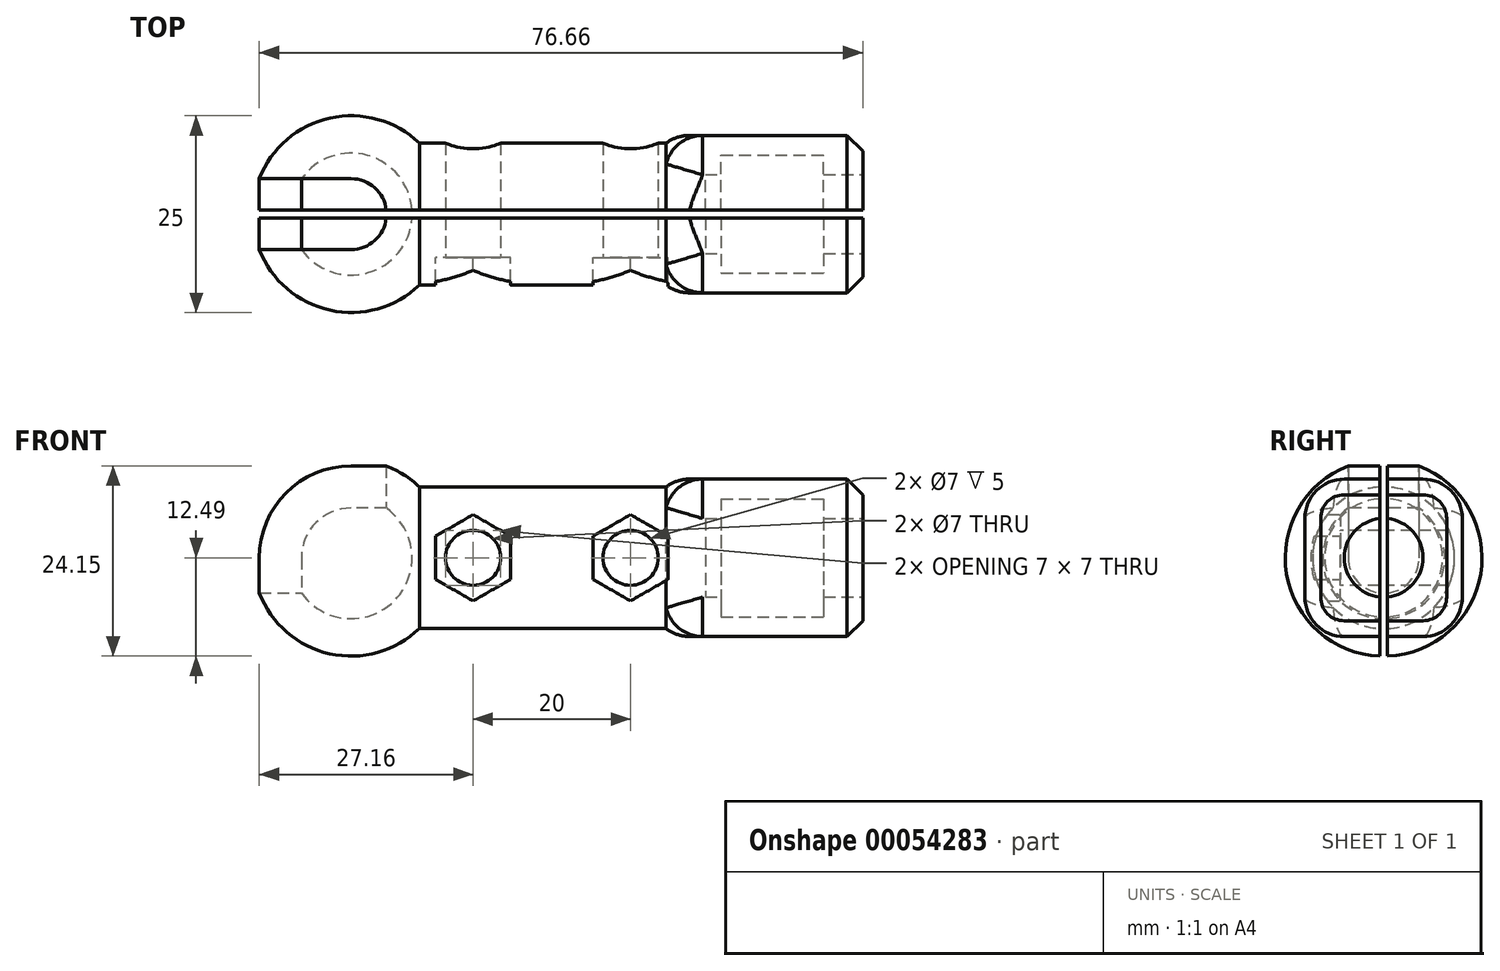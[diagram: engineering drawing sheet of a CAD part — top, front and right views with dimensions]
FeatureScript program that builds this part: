
annotation { "Feature Type Name" : "Feature", "Feature Type Description" : "" }
export const myFeature = defineFeature(function(context is Context, id is Id, definition is map)
    precondition{}
    {
        {
            var Q0;
            Q0=qCreatedBy(makeId("Top.planeOp"),FACE);
            var sketch = newSketch(context, id + "F0", { "sketchPlane" : qUnion([Q0])});
            skLineSegment(sketch, "E0.bottom", {"start": v(0, 0) * mm, "end": v(25, 0) * mm});
            skLineSegment(sketch, "E0.top", {"start": v(0, 25) * mm, "end": v(25, 25) * mm});
            skLineSegment(sketch, "E0.left", {"start": v(0, 0) * mm, "end": v(0, 25) * mm});
            skLineSegment(sketch, "E0.right", {"start": v(25, 0) * mm, "end": v(25, 25) * mm});
            skSolve(sketch);
        }
        {
            var Q0;
            Q0 = qSketchRegion(id + "F0", true);
            extrude(context, id + "F1", {"entities" : qUnion([Q0]), "depth" : 25 * mm});
        }
        {
            var Q0;
            Q0=makeQuery(id+"F1.opExtrude","CAP_EDGE",EDGE,{"disambiguationData":[OSD([sQuery(id+"F0.wireOp",EDGE,"E0.left")])],"isStart":false});
            var Q1;
            Q1=makeQuery(id+"F1.opExtrude","CAP_EDGE",EDGE,{"disambiguationData":[OSD([sQuery(id+"F0.wireOp",EDGE,"E0.right")])],"isStart":false});
            var Q2;
            Q2=makeQuery(id+"F1.opExtrude","CAP_EDGE",EDGE,{"disambiguationData":[OSD([sQuery(id+"F0.wireOp",EDGE,"E0.right")])],"isStart":true});
            var Q3;
            Q3=makeQuery(id+"F1.opExtrude","CAP_FACE",FACE,{"disambiguationData":[OSD([sQuery(id+"F0.wireOp",EDGE,"E0.bottom"),sQuery(id+"F0.wireOp",EDGE,"E0.top"),sQuery(id+"F0.wireOp",EDGE,"E0.left"),sQuery(id+"F0.wireOp",EDGE,"E0.right")])],"isStart":true});
            var Q4;
            Q4=makeQuery(id+"F1.opExtrude","SWEPT_EDGE",EDGE,{"disambiguationData":[OSD([sQuery(id+"F0.wireOp",EDGE,"E0.bottom"),sQuery(id+"F0.wireOp",EDGE,"E0.left")])]});
            var Q5;
            Q5=makeQuery(id+"F1.opExtrude","SWEPT_EDGE",EDGE,{"disambiguationData":[OSD([sQuery(id+"F0.wireOp",EDGE,"E0.top"),sQuery(id+"F0.wireOp",EDGE,"E0.left")])]});
            var Q6;
            Q6=makeQuery(id+"F1.opExtrude","CAP_EDGE",EDGE,{"disambiguationData":[OSD([sQuery(id+"F0.wireOp",EDGE,"E0.top")])],"isStart":true});
            var Q7;
            Q7=makeQuery(id+"F1.opExtrude","CAP_EDGE",EDGE,{"disambiguationData":[OSD([sQuery(id+"F0.wireOp",EDGE,"E0.left")])],"isStart":true});
            var Q8;
            Q8=makeQuery(id+"F1.opExtrude","CAP_EDGE",EDGE,{"disambiguationData":[OSD([sQuery(id+"F0.wireOp",EDGE,"E0.bottom")])],"isStart":false});
            var Q9;
            Q9=makeQuery(id+"F1.opExtrude","CAP_EDGE",EDGE,{"disambiguationData":[OSD([sQuery(id+"F0.wireOp",EDGE,"E0.top")])],"isStart":false});
            var Q10;
            Q10=makeQuery(id+"F1.opExtrude","SWEPT_EDGE",EDGE,{"disambiguationData":[OSD([sQuery(id+"F0.wireOp",EDGE,"E0.top"),sQuery(id+"F0.wireOp",EDGE,"E0.right")])]});
            var Q11;
            Q11=makeQuery(id+"F1.opExtrude","SWEPT_EDGE",EDGE,{"disambiguationData":[OSD([sQuery(id+"F0.wireOp",EDGE,"E0.bottom"),sQuery(id+"F0.wireOp",EDGE,"E0.right")])]});
            fillet(context, id + "F2", {"entities" : qUnion([Q0, Q1, Q2, Q3, Q4, Q5, Q6, Q7, Q8, Q9, Q10, Q11]), "radius" : 12.5 * mm, "tangentPropagation" : true, "allowEdgeOverflow" : false});
        }
        {
            var Q0;
            Q0=qCreatedBy(makeId("Right.planeOp"),FACE);
            cPlane(context, id + "F3", {"entities" : qUnion([Q0]), "cplaneType" : CPlaneType.OFFSET, "offset" : 12.5 * mm, "width" : 150 * mm, "height" : 150 * mm});
        }
        {
            var Q0;
            Q0=qCreatedBy(id+"F3.planeOp",FACE);
            var sketch = newSketch(context, id + "F4", { "sketchPlane" : qUnion([Q0])});
            skCircle(sketch, "E1", {"center": v(12.5, 12.5) * mm, "radius": 9 * mm});
            skSolve(sketch);
        }
        {
            var Q0;
            Q0 = qSketchRegion(id + "F4", true);
            extrude(context, id + "F5", {"entities" : qUnion([Q0]), "operationType" : NewBodyOperationType.ADD, "depth" : 40 * mm});
        }
        {
            var Q0;
            Q0=makeQuery(id+"F5.opExtrude","CAP_FACE",FACE,{"disambiguationData":[OSD([sQuery(id+"F4.wireOp",EDGE,"E1")])],"isStart":false});
            var sketch = newSketch(context, id + "F6", { "sketchPlane" : qUnion([Q0])});
            skLineSegment(sketch, "E2.bottom", {"start": v(2.5, 22.5) * mm, "end": v(22.5, 22.5) * mm});
            skLineSegment(sketch, "E2.top", {"start": v(2.5, 2.5) * mm, "end": v(22.5, 2.5) * mm});
            skLineSegment(sketch, "E2.left", {"start": v(2.5, 22.5) * mm, "end": v(2.5, 2.5) * mm});
            skLineSegment(sketch, "E2.right", {"start": v(22.5, 22.5) * mm, "end": v(22.5, 2.5) * mm});
            skPoint(sketch, "E3", {"position": v(12.5, 12.5) * mm});
            skSolve(sketch);
        }
        {
            var Q0;
            Q0 = qSketchRegion(id + "F6", true);
            extrude(context, id + "F7", {"entities" : qUnion([Q0]), "operationType" : NewBodyOperationType.ADD, "depth" : 25 * mm});
        }
        {
            var Q0;
            Q0=makeQuery(id+"F7.opExtrude","SWEPT_EDGE",EDGE,{"disambiguationData":[OSD([sQuery(id+"F6.wireOp",EDGE,"E2.bottom"),sQuery(id+"F6.wireOp",EDGE,"E2.left")])]});
            var Q1;
            Q1=makeQuery(id+"F7.opExtrude","SWEPT_EDGE",EDGE,{"disambiguationData":[OSD([sQuery(id+"F6.wireOp",EDGE,"E2.bottom"),sQuery(id+"F6.wireOp",EDGE,"E2.right")])]});
            var Q2;
            Q2=makeQuery(id+"F7.opExtrude","SWEPT_EDGE",EDGE,{"disambiguationData":[OSD([sQuery(id+"F6.wireOp",EDGE,"E2.top"),sQuery(id+"F6.wireOp",EDGE,"E2.right")])]});
            var Q3;
            Q3=makeQuery(id+"F7.opExtrude","SWEPT_EDGE",EDGE,{"disambiguationData":[OSD([sQuery(id+"F6.wireOp",EDGE,"E2.top"),sQuery(id+"F6.wireOp",EDGE,"E2.left")])]});
            fillet(context, id + "F8", {"entities" : qUnion([Q0, Q1, Q2, Q3]), "radius" : 5 * mm, "tangentPropagation" : true, "allowEdgeOverflow" : false});
        }
        {
            var Q0;
            Q0=qCreatedBy(makeId("Top.planeOp"),FACE);
            var sketch = newSketch(context, id + "F9", { "sketchPlane" : qUnion([Q0])});
            skLineSegment(sketch, "E4.bottom", {"start": v(0, 12) * mm, "end": v(80, 12) * mm});
            skLineSegment(sketch, "E4.top", {"start": v(0, 13) * mm, "end": v(80, 13) * mm});
            skLineSegment(sketch, "E4.left", {"start": v(0, 12) * mm, "end": v(0, 13) * mm});
            skLineSegment(sketch, "E4.right", {"start": v(80, 12) * mm, "end": v(80, 13) * mm});
            skSolve(sketch);
        }
        {
            var Q0;
            Q0 = qSketchRegion(id + "F9", true);
            extrude(context, id + "F10", {"entities" : qUnion([Q0]), "operationType" : NewBodyOperationType.REMOVE, "endBound" : BoundingType.THROUGH_ALL, "depth" : 29.4 * mm});
        }
        {
            var Q0;
            {var subQ0=sQuery(id+"F6.wireOp",EDGE,"E2.right");var subQ1=sQuery(id+"F6.wireOp",EDGE,"E2.bottom");Q0=makeQuery(id+"F8.opFillet","BLEND_EDGE",EDGE,{"blendedFrom":[makeQuery(id+"F7.opExtrude","SWEPT_EDGE",EDGE,{"disambiguationData":[OSD([subQ1,subQ0])]}),makeQuery(id+"F7.opExtrude","CAP_FACE",FACE,{"disambiguationData":[OSD([subQ1,sQuery(id+"F6.wireOp",EDGE,"E2.top"),sQuery(id+"F6.wireOp",EDGE,"E2.left"),subQ0])],"isStart":true})],"blendedInto":[makeQuery(id+"F7.opExtrude","CAP_FACE",FACE,{"disambiguationData":[OSD([subQ1,sQuery(id+"F6.wireOp",EDGE,"E2.top"),sQuery(id+"F6.wireOp",EDGE,"E2.left"),subQ0])],"isStart":true})]});}
            var Q1;
            {var subQ0=sQuery(id+"F6.wireOp",EDGE,"E2.left");var subQ1=sQuery(id+"F6.wireOp",EDGE,"E2.bottom");Q1=makeQuery(id+"F8.opFillet","BLEND_EDGE",EDGE,{"blendedFrom":[makeQuery(id+"F7.opExtrude","SWEPT_EDGE",EDGE,{"disambiguationData":[OSD([subQ1,subQ0])]}),makeQuery(id+"F7.opExtrude","CAP_FACE",FACE,{"disambiguationData":[OSD([subQ1,sQuery(id+"F6.wireOp",EDGE,"E2.top"),subQ0,sQuery(id+"F6.wireOp",EDGE,"E2.right")])],"isStart":true})],"blendedInto":[makeQuery(id+"F7.opExtrude","CAP_FACE",FACE,{"disambiguationData":[OSD([subQ1,sQuery(id+"F6.wireOp",EDGE,"E2.top"),subQ0,sQuery(id+"F6.wireOp",EDGE,"E2.right")])],"isStart":true})]});}
            fillet(context, id + "F11", {"entities" : qUnion([Q0, Q1]), "radius" : 5 * mm, "tangentPropagation" : true, "allowEdgeOverflow" : false});
        }
        {
            var Q0;
            {var subQ0=sQuery(id+"F6.wireOp",EDGE,"E2.left");var subQ1=sQuery(id+"F6.wireOp",EDGE,"E2.bottom");var subQ2=sQuery(id+"F6.wireOp",EDGE,"E2.top");Q0=makeQuery(id+"F10.boolean.opBoolean","SPLIT",FACE,{"disambiguationData":[TD([makeQuery(id+"F7.opExtrude","SWEPT_FACE",FACE,{"disambiguationData":[OSD([subQ0])]})])],"derivedFrom":makeQuery(id+"F7.opExtrude","CAP_FACE",FACE,{"disambiguationData":[OSD([subQ1,subQ2,subQ0,sQuery(id+"F6.wireOp",EDGE,"E2.right")])],"isStart":false})});}
            var sketch = newSketch(context, id + "F12", { "sketchPlane" : qUnion([Q0])});
            skCircle(sketch, "E5", {"center": v(12.5, 12.5) * mm, "radius": 5 * mm});
            skSolve(sketch);
        }
        {
            var Q0;
            Q0 = qSketchRegion(id + "F12", true);
            extrude(context, id + "F13", {"entities" : qUnion([Q0]), "operationType" : NewBodyOperationType.REMOVE, "oppositeDirection" : true, "depth" : 20 * mm});
        }
        {
            var Q0;
            {var subQ0=sQuery(id+"F6.wireOp",EDGE,"E2.right");var subQ1=sQuery(id+"F6.wireOp",EDGE,"E2.bottom");var subQ2=sQuery(id+"F6.wireOp",EDGE,"E2.top");Q0=makeQuery(id+"F10.boolean.opBoolean","SPLIT",FACE,{"disambiguationData":[TD([makeQuery(id+"F7.opExtrude","SWEPT_FACE",FACE,{"disambiguationData":[OSD([subQ0])]})])],"derivedFrom":makeQuery(id+"F7.opExtrude","CAP_FACE",FACE,{"disambiguationData":[OSD([subQ1,subQ2,sQuery(id+"F6.wireOp",EDGE,"E2.left"),subQ0])],"isStart":false})});}
            cPlane(context, id + "F14", {"entities" : qUnion([Q0]), "cplaneType" : CPlaneType.OFFSET, "offset" : 5 * mm, "oppositeDirection" : true, "width" : 150 * mm, "height" : 150 * mm});
        }
        {
            var Q0;
            Q0=qCreatedBy(id+"F14.planeOp",FACE);
            var sketch = newSketch(context, id + "F15", { "sketchPlane" : qUnion([Q0])});
            skCircle(sketch, "E6", {"center": v(12.5, 12.5) * mm, "radius": 7.5 * mm});
            skSolve(sketch);
        }
        {
            var Q0;
            Q0 = qSketchRegion(id + "F15", true);
            extrude(context, id + "F16", {"entities" : qUnion([Q0]), "operationType" : NewBodyOperationType.REMOVE, "oppositeDirection" : true, "depth" : 13 * mm});
        }
        {
            var Q0;
            Q0=qCreatedBy(id+"F3.planeOp",FACE);
            var sketch = newSketch(context, id + "F17", { "sketchPlane" : qUnion([Q0])});
            skArc(sketch, "E7", {"start": v(12.5, 4.75) * mm, "mid": v(20.25, 12.5) * mm, "end": v(12.5, 20.25) * mm});
            skLineSegment(sketch, "E8", {"start": v(12.5, 20.25) * mm, "end": v(12.5, 4.75) * mm});
            skSolve(sketch);
        }
        {
            var Q0;
            Q0 = qSketchRegion(id + "F17", true);
            var Q1;
            Q1=sQuery(id+"F17.wireOp",EDGE,"E8");
            revolve(context, id + "F18", {"operationType" : NewBodyOperationType.REMOVE, "entities" : qUnion([Q0]), "axis" : qUnion([Q1]), "revolveType" : RevolveType.FULL, "oppositeDirection" : true});
        }
        {
            var Q0;
            Q0=qCreatedBy(id+"F3.planeOp",FACE);
            var sketch = newSketch(context, id + "F19", { "sketchPlane" : qUnion([Q0])});
            skCircle(sketch, "E9", {"center": v(12.5, 12.5) * mm, "radius": 4.5 * mm});
            skSolve(sketch);
        }
        {
            var Q0;
            Q0 = qSketchRegion(id + "F19", true);
            extrude(context, id + "F20", {"entities" : qUnion([Q0]), "operationType" : NewBodyOperationType.REMOVE, "oppositeDirection" : true, "depth" : 25 * mm});
        }
        {
            var Q0;
            Q0=qCreatedBy(makeId("Top.planeOp"),FACE);
            cPlane(context, id + "F21", {"entities" : qUnion([Q0]), "cplaneType" : CPlaneType.OFFSET, "offset" : 12.5 * mm, "width" : 150 * mm, "height" : 150 * mm});
        }
        {
            var Q0;
            Q0=qCreatedBy(id+"F21.planeOp",FACE);
            var sketch = newSketch(context, id + "F22", { "sketchPlane" : qUnion([Q0])});
            skCircle(sketch, "E10", {"center": v(12.5, 12.5) * mm, "radius": 4.5 * mm});
            skSolve(sketch);
        }
        {
            var Q0;
            Q0 = qSketchRegion(id + "F22", true);
            extrude(context, id + "F23", {"entities" : qUnion([Q0]), "operationType" : NewBodyOperationType.REMOVE, "depth" : 25 * mm});
        }
        {
            var Q0;
            Q0=qCreatedBy(id+"F21.planeOp",FACE);
            var sketch = newSketch(context, id + "F24", { "sketchPlane" : qUnion([Q0])});
            skLineSegment(sketch, "E11.bottom", {"start": v(12.5, 8) * mm, "end": v(0, 8) * mm});
            skLineSegment(sketch, "E11.top", {"start": v(12.5, 17) * mm, "end": v(0, 17) * mm});
            skLineSegment(sketch, "E11.left", {"start": v(12.5, 8) * mm, "end": v(12.5, 17) * mm});
            skLineSegment(sketch, "E11.right", {"start": v(0, 8) * mm, "end": v(0, 17) * mm});
            skSolve(sketch);
        }
        {
            var Q0;
            Q0 = qSketchRegion(id + "F24", true);
            var Q1;
            Q1=sQuery(id+"F24.wireOp",EDGE,"E11.left");
            revolve(context, id + "F25", {"operationType" : NewBodyOperationType.REMOVE, "entities" : qUnion([Q0]), "axis" : qUnion([Q1]), "revolveType" : RevolveType.ONE_DIRECTION, "angle" : 90 * degree});
        }
        {
            var Q0;
            Q0=qCreatedBy(makeId("Front.planeOp"),FACE);
            var sketch = newSketch(context, id + "F26", { "sketchPlane" : qUnion([Q0])});
            skCircle(sketch, "E12", {"center": v(28, 12.5) * mm, "radius": 3.5 * mm});
            skCircle(sketch, "E13", {"center": v(48, 12.5) * mm, "radius": 3.5 * mm});
            skSolve(sketch);
        }
        {
            var Q0;
            Q0 = qSketchRegion(id + "F26", true);
            extrude(context, id + "F27", {"entities" : qUnion([Q0]), "operationType" : NewBodyOperationType.REMOVE, "oppositeDirection" : true, "depth" : 25 * mm});
        }
        {
            var Q0;
            {var subQ0=sQuery(id+"F6.wireOp",EDGE,"E2.bottom");Q0=makeQuery(id+"F10.boolean.opBoolean","SPLIT",EDGE,{"disambiguationData":[TD([makeQuery(id+"F10.opExtrude","SWEPT_FACE",FACE,{"disambiguationData":[OSD([sQuery(id+"F9.wireOp",EDGE,"E4.bottom")])]})])],"derivedFrom":makeQuery(id+"F7.opExtrude","CAP_EDGE",EDGE,{"disambiguationData":[OSD([subQ0])],"isStart":false})});}
            var Q1;
            {var subQ0=sQuery(id+"F6.wireOp",EDGE,"E2.bottom");Q1=makeQuery(id+"F10.boolean.opBoolean","SPLIT",EDGE,{"disambiguationData":[TD([makeQuery(id+"F10.opExtrude","SWEPT_FACE",FACE,{"disambiguationData":[OSD([sQuery(id+"F9.wireOp",EDGE,"E4.top")])]})])],"derivedFrom":makeQuery(id+"F7.opExtrude","CAP_EDGE",EDGE,{"disambiguationData":[OSD([subQ0])],"isStart":false})});}
            chamfer(context, id + "F28", {"entities" : qUnion([Q0, Q1]), "width" : 2 * mm, "tangentPropagation" : true});
        }
        {
            var Q0;
            Q0=qCreatedBy(makeId("Front.planeOp"),FACE);
            cPlane(context, id + "F29", {"entities" : qUnion([Q0]), "cplaneType" : CPlaneType.OFFSET, "offset" : 7 * mm, "oppositeDirection" : true, "width" : 150 * mm, "height" : 150 * mm});
        }
        {
            var Q0;
            Q0=qCreatedBy(id+"F29.planeOp",FACE);
            var sketch = newSketch(context, id + "F30", { "sketchPlane" : qUnion([Q0])});
            skCircle(sketch, "E14.cCircle", {"center": v(48, 12.5) * mm, "radius": 4.75 * mm, "construction": true});
            skLineSegment(sketch, "E14.0", {"start": v(48, 17.98) * mm, "end": v(52.75, 15.24) * mm});
            skLineSegment(sketch, "E14.1", {"start": v(52.75, 15.24) * mm, "end": v(52.75, 9.76) * mm});
            skLineSegment(sketch, "E14.2", {"start": v(52.75, 9.76) * mm, "end": v(48, 7.02) * mm});
            skLineSegment(sketch, "E14.3", {"start": v(48, 7.02) * mm, "end": v(43.25, 9.76) * mm});
            skLineSegment(sketch, "E14.4", {"start": v(43.25, 9.76) * mm, "end": v(43.25, 15.24) * mm});
            skLineSegment(sketch, "E14.5", {"start": v(43.25, 15.24) * mm, "end": v(48, 17.98) * mm});
            skPoint(sketch, "E14.0.midPoint", {"position": v(50.38, 16.61) * mm});
            skLineSegment(sketch, "E15.2", {"start": v(32.75, 9.76) * mm, "end": v(28, 7.02) * mm});
            skLineSegment(sketch, "E15.3", {"start": v(28, 7.02) * mm, "end": v(23.25, 9.76) * mm});
            skLineSegment(sketch, "E15.4", {"start": v(23.25, 9.76) * mm, "end": v(23.25, 15.24) * mm});
            skCircle(sketch, "E15.cCircle", {"center": v(28, 12.5) * mm, "radius": 4.75 * mm, "construction": true});
            skLineSegment(sketch, "E15.0", {"start": v(28, 17.98) * mm, "end": v(32.75, 15.24) * mm});
            skLineSegment(sketch, "E15.5", {"start": v(23.25, 15.24) * mm, "end": v(28, 17.98) * mm});
            skLineSegment(sketch, "E15.1", {"start": v(32.75, 15.24) * mm, "end": v(32.75, 9.76) * mm});
            skPoint(sketch, "E15.0.midPoint", {"position": v(30.38, 16.61) * mm});
            skSolve(sketch);
        }
        {
            var Q0;
            Q0 = qSketchRegion(id + "F30", true);
            extrude(context, id + "F31", {"entities" : qUnion([Q0]), "operationType" : NewBodyOperationType.REMOVE, "depth" : 8.37 * mm});
        }
    });
